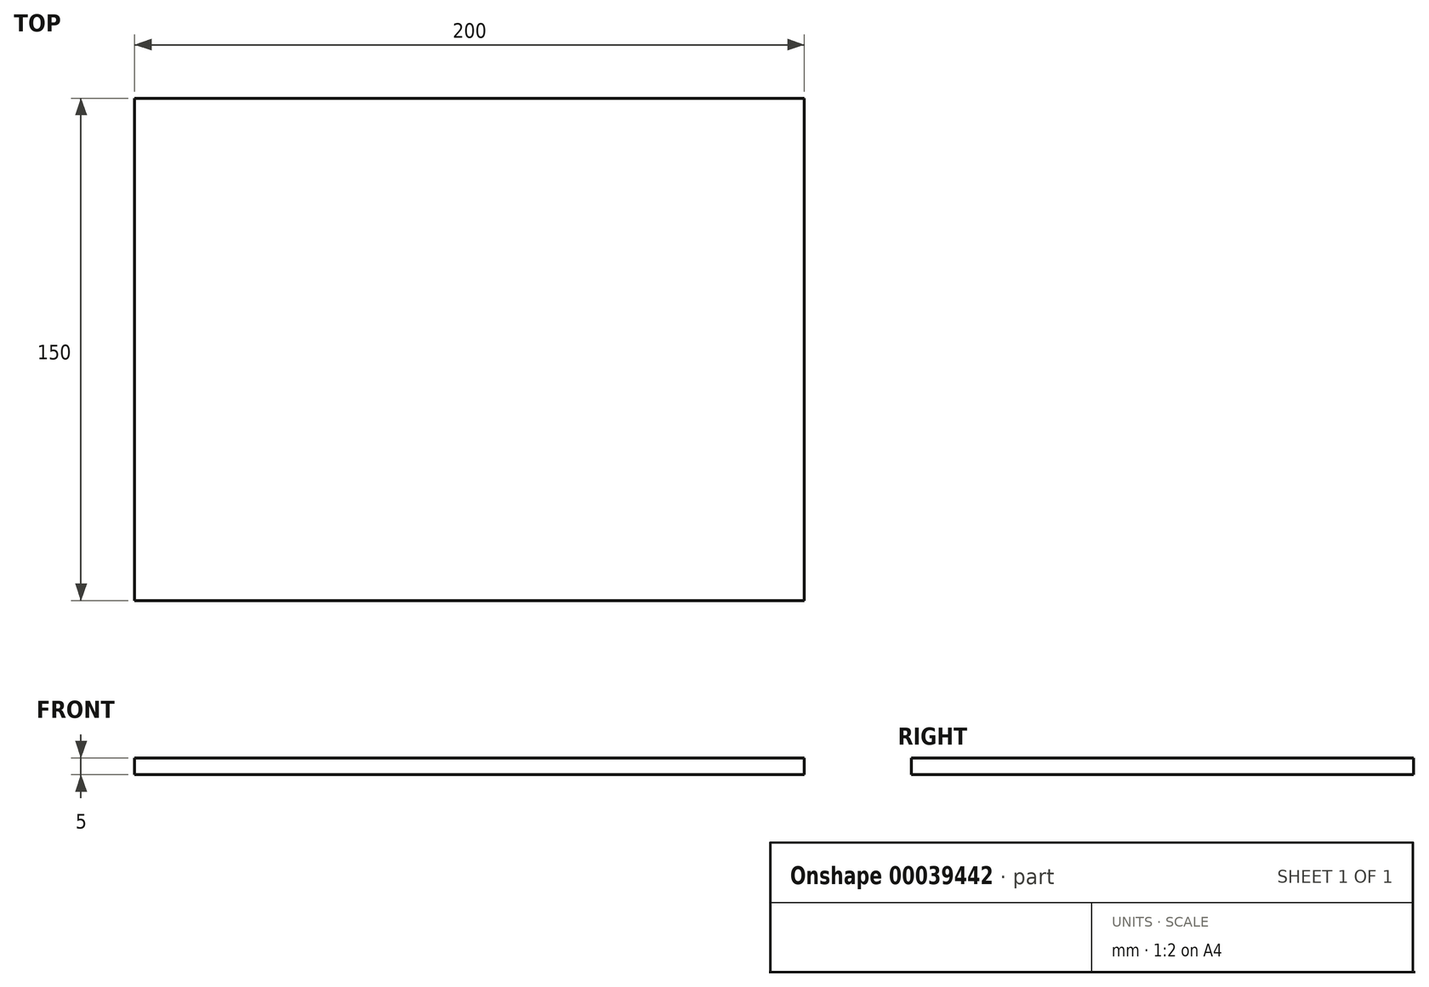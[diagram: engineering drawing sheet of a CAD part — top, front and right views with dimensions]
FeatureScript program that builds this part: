
annotation { "Feature Type Name" : "Feature", "Feature Type Description" : "" }
export const myFeature = defineFeature(function(context is Context, id is Id, definition is map)
    precondition{}
    {
        {
            var Q0;
            Q0=qCreatedBy(makeId("Top.planeOp"),FACE);
            var sketch = newSketch(context, id + "F0", { "sketchPlane" : qUnion([Q0])});
            skLineSegment(sketch, "E0.bottom", {"start": v(-100, 75) * mm, "end": v(100, 75) * mm});
            skLineSegment(sketch, "E0.top", {"start": v(-100, -75) * mm, "end": v(100, -75) * mm});
            skLineSegment(sketch, "E0.left", {"start": v(-100, 75) * mm, "end": v(-100, -75) * mm});
            skLineSegment(sketch, "E0.right", {"start": v(100, 75) * mm, "end": v(100, -75) * mm});
            skLineSegment(sketch, "E1", {"start": v(-100, -75) * mm, "end": v(100, 75) * mm, "construction": true});
            skSolve(sketch);
        }
        {
            var Q0;
            Q0=makeQuery(id+"F0.imprint","IMPRINT",FACE,{"disambiguationData":[TD([[makeQuery(id+"F0.imprint","IMPRINT",EDGE,{"derivedFrom":sQuery(id+"F0.wireOp",EDGE,"E0.bottom")}),-1.0]])]});
            extrude(context, id + "F1", {"entities" : qUnion([Q0]), "oppositeDirection" : true, "depth" : 5 * mm});
        }
    });
